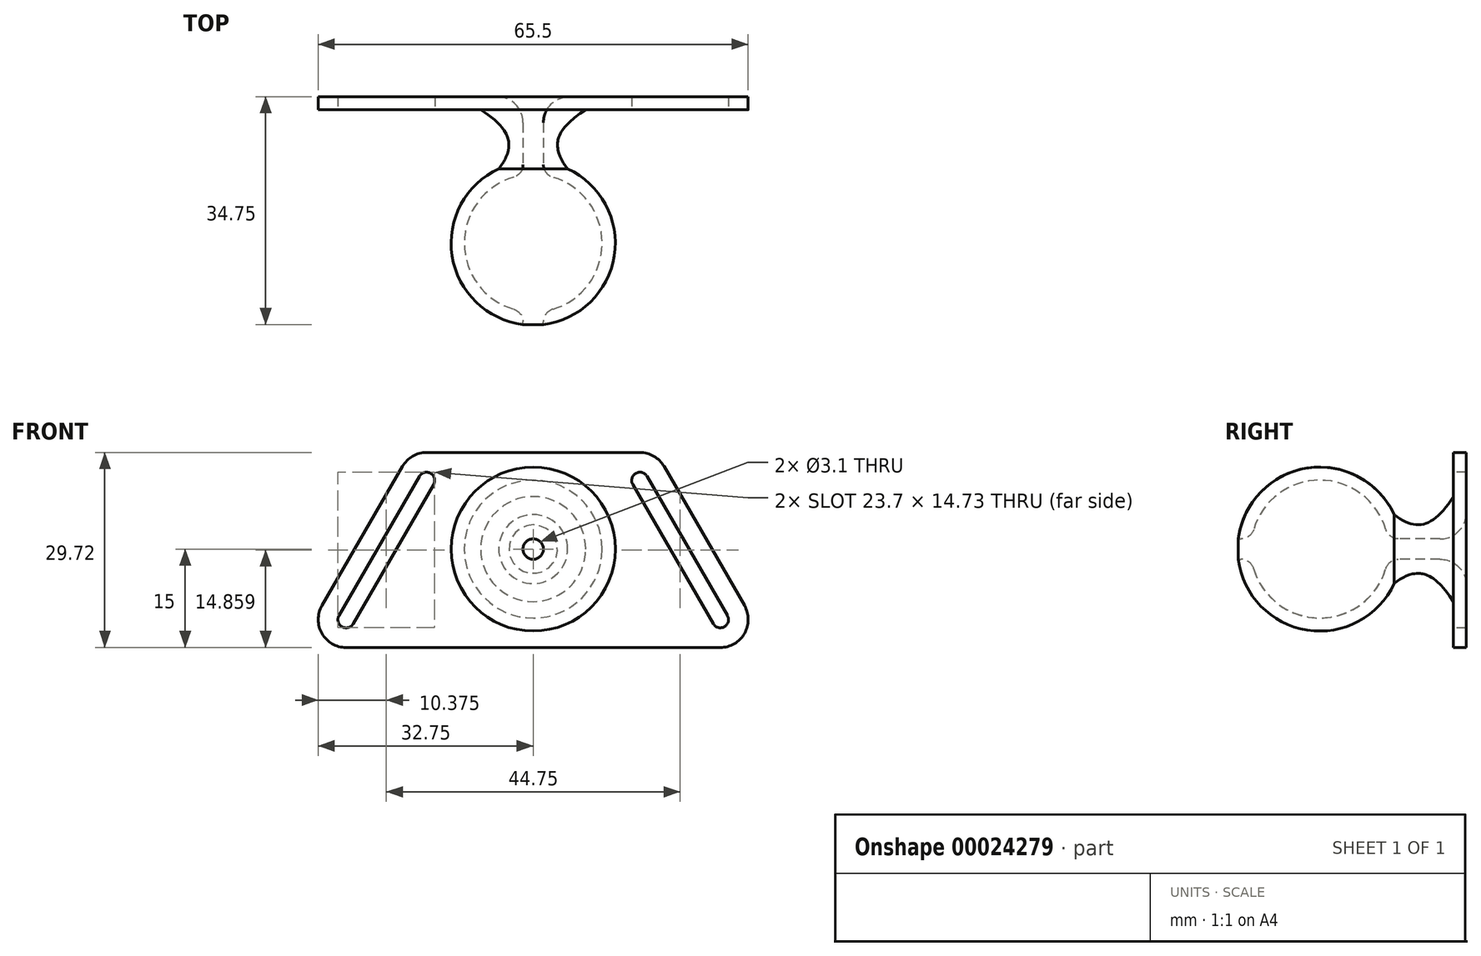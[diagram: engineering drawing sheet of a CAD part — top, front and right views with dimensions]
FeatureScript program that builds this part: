
annotation { "Feature Type Name" : "Feature", "Feature Type Description" : "" }
export const myFeature = defineFeature(function(context is Context, id is Id, definition is map)
    precondition{}
    {
        {
            var Q0;
            Q0=qCreatedBy(makeId("Front.planeOp"),FACE);
            var sketch = newSketch(context, id + "F0", { "sketchPlane" : qUnion([Q0])});
            skLineSegment(sketch, "E0", {"start": v(0, 0) * mm, "end": v(-28.5, 0) * mm});
            skLineSegment(sketch, "E1", {"start": v(0, 0) * mm, "end": v(0, 29.72) * mm});
            skLineSegment(sketch, "E2", {"start": v(-16.25, 25.47) * mm, "end": v(-28.5, 4.25) * mm, "construction": true});
            skCircle(sketch, "E3", {"center": v(-28.5, 4.25) * mm, "radius": 1.25 * mm});
            skCircle(sketch, "E4", {"center": v(-16.25, 25.47) * mm, "radius": 1.25 * mm});
            skLineSegment(sketch, "E5", {"start": v(-29.58, 4.87) * mm, "end": v(-17.33, 26.1) * mm});
            skLineSegment(sketch, "E6", {"start": v(-15.17, 24.84) * mm, "end": v(-27.42, 3.62) * mm});
            skCircle(sketch, "E7.0", {"center": v(-28.5, 4.25) * mm, "radius": 4.25 * mm});
            skCircle(sketch, "E8.0", {"center": v(-16.25, 25.47) * mm, "radius": 4.25 * mm});
            skLineSegment(sketch, "E9", {"start": v(-32.18, 6.37) * mm, "end": v(-19.93, 27.6) * mm});
            skLineSegment(sketch, "E10", {"start": v(-16.25, 29.72) * mm, "end": v(0, 29.72) * mm});
            skPoint(sketch, "E11", {"position": v(0, 15) * mm});
            skArc(sketch, "E12", {"start": v(0, 16.55) * mm, "mid": v(-1.55, 15) * mm, "end": v(0, 13.45) * mm});
            skSolve(sketch);
        }
        {
            var Q0;
            {var subQ3=sQuery(id+"F0.wireOp",EDGE,"E9");Q0=makeQuery(id+"F0.imprint","IMPRINT",FACE,{"disambiguationData":[TD([[makeQuery(id+"F0.imprint","IMPRINT",EDGE,{"derivedFrom":subQ3}),-1.0]])]});}
            var Q1;
            {var subQ5=sQuery(id+"F0.wireOp",EDGE,"E5");var subQ7=sQuery(id+"F0.wireOp",EDGE,"E3");var subQ9=makeQuery(id+"F0.imprint","INTERSECT",VERTEX,{"derivedFrom":[subQ7,subQ5]});Q1=makeQuery(id+"F0.imprint","IMPRINT",FACE,{"disambiguationData":[TD([[makeQuery(id+"F0.imprint","IMPRINT",EDGE,{"disambiguationData":[TD([[subQ9,-1.0]])],"derivedFrom":subQ7}),-1.0]])]});}
            var Q2;
            {var subQ4=sQuery(id+"F0.wireOp",EDGE,"E5");var subQ7=sQuery(id+"F0.wireOp",EDGE,"E4");var subQ9=makeQuery(id+"F0.imprint","INTERSECT",VERTEX,{"derivedFrom":[subQ7,subQ4]});Q2=makeQuery(id+"F0.imprint","IMPRINT",FACE,{"disambiguationData":[TD([[makeQuery(id+"F0.imprint","IMPRINT",EDGE,{"disambiguationData":[TD([[subQ9,1.0]])],"derivedFrom":subQ7}),-1.0]])]});}
            var Q3;
            {var subQ6=sQuery(id+"F0.wireOp",EDGE,"E0");Q3=makeQuery(id+"F0.imprint","IMPRINT",FACE,{"disambiguationData":[TD([[makeQuery(id+"F0.imprint","IMPRINT",EDGE,{"derivedFrom":subQ6}),-1.0]])]});}
            extrude(context, id + "F1", {"entities" : qUnion([Q0, Q1, Q2, Q3]), "oppositeDirection" : true, "depth" : 2 * mm});
        }
        {
            var Q0;
            Q0=makeQuery(id+"F1.opExtrude","SWEPT_BODY",BODY,{"disambiguationData":[OSD([sQuery(id+"F0.wireOp",EDGE,"E0"),sQuery(id+"F0.wireOp",EDGE,"E1"),sQuery(id+"F0.wireOp",EDGE,"E3"),sQuery(id+"F0.wireOp",EDGE,"E4"),sQuery(id+"F0.wireOp",EDGE,"E5"),sQuery(id+"F0.wireOp",EDGE,"E6"),sQuery(id+"F0.wireOp",EDGE,"E7.0"),sQuery(id+"F0.wireOp",EDGE,"E8.0"),sQuery(id+"F0.wireOp",EDGE,"E9"),sQuery(id+"F0.wireOp",EDGE,"E10")])]});
            var Q1;
            Q1=makeQuery(id+"F1.opExtrude","SWEPT_FACE",FACE,{"disambiguationData":[OSD([sQuery(id+"F0.wireOp",EDGE,"E1")])]});
            mirror(context, id + "F2", {"operationType" : NewBodyOperationType.ADD, "entities" : qUnion([Q0]), "mirrorPlane" : qUnion([Q1])});
        }
        {
            var Q0;
            Q0=qCreatedBy(makeId("Right.planeOp"),FACE);
            var sketch = newSketch(context, id + "F3", { "sketchPlane" : qUnion([Q0])});
            skLineSegment(sketch, "E13", {"start": v(0, 15) * mm, "end": v(-32.84, 15) * mm});
            skArc(sketch, "E14", {"start": v(-32.84, 15) * mm, "mid": v(-20.34, 2.5) * mm, "end": v(-7.84, 15) * mm});
            skLineSegment(sketch, "E15", {"start": v(-9, 15) * mm, "end": v(-9, 9.75) * mm});
            skFitSpline(sketch, "E16", {"points": [v(-9, 9.75) * mm, v(0, 7) * mm], "startDerivative": vector(10.27, 8.04) * mm, "endDerivative": vector(9.03, -14.12) * mm});
            skLineSegment(sketch, "E17", {"start": v(-32.75, 13.45) * mm, "end": v(0, 13.45) * mm});
            skPoint(sketch, "E18.0", {"position": v(0, 15) * mm});
            skLineSegment(sketch, "E19", {"start": v(0, 15) * mm, "end": v(0, 7) * mm});
            skLineSegment(sketch, "E20.0", {"start": v(0, 13.45) * mm, "end": v(0, 16.55) * mm});
            skCircle(sketch, "E21", {"center": v(-20.34, 15) * mm, "radius": 10.5 * mm});
            skSolve(sketch);
        }
        {
            var Q0;
            {var subQ4=sQuery(id+"F3.wireOp",EDGE,"E16");Q0=makeQuery(id+"F3.imprint","IMPRINT",FACE,{"disambiguationData":[TD([[makeQuery(id+"F3.imprint","IMPRINT",EDGE,{"derivedFrom":subQ4}),1.0]])]});}
            var Q1;
            {var subQ0=sQuery(id+"F3.wireOp",EDGE,"E17");var subQ3=sQuery(id+"F3.wireOp",EDGE,"E14");var subQ4=makeQuery(id+"F3.imprint","INTERSECT",VERTEX,{"derivedFrom":[subQ3,subQ0]});Q1=makeQuery(id+"F3.imprint","IMPRINT",FACE,{"disambiguationData":[TD([[makeQuery(id+"F3.imprint","IMPRINT",EDGE,{"disambiguationData":[TD([[subQ4,1.0]])],"derivedFrom":subQ0}),-1.0]])]});}
            var Q2;
            {var subQ3=sQuery(id+"F3.wireOp",EDGE,"bf7e747b-2e18-4020-b302-44ba4e78f57e");var subQ5=sQuery(id+"F3.wireOp",EDGE,"E14");var subQ6=makeQuery(id+"F3.imprint","INTERSECT",VERTEX,{"derivedFrom":[subQ5,subQ3]});Q2=makeQuery(id+"F3.imprint","IMPRINT",FACE,{"disambiguationData":[TD([[makeQuery(id+"F3.imprint","IMPRINT",EDGE,{"disambiguationData":[TD([[subQ6,1.0]])],"derivedFrom":subQ3}),1.0]])]});}
            var Q3;
            {var subQ1=sQuery(id+"F3.wireOp",EDGE,"E17");var subQ6=sQuery(id+"F3.wireOp",EDGE,"E14");var subQ7=makeQuery(id+"F3.imprint","INTERSECT",VERTEX,{"disambiguationData":[OD(0.0)],"derivedFrom":[subQ6,subQ1]});Q3=makeQuery(id+"F3.imprint","IMPRINT",FACE,{"disambiguationData":[TD([[makeQuery(id+"F3.imprint","IMPRINT",EDGE,{"disambiguationData":[TD([[subQ7,-1.0]])],"derivedFrom":subQ1}),-1.0]])]});}
            var Q4;
            Q4=sQuery(id+"F3.wireOp",EDGE,"E13");
            revolve(context, id + "F4", {"operationType" : NewBodyOperationType.ADD, "entities" : qUnion([Q0, Q1, Q2, Q3]), "axis" : qUnion([Q4]), "revolveType" : RevolveType.FULL});
        }
        {
            var Q0;
            {var subQ0=makeQuery(id+"F1.opExtrude","CAP_EDGE",EDGE,{"disambiguationData":[OSD([sQuery(id+"F0.wireOp",EDGE,"E12")])],"isStart":false});Q0=makeQuery(id+"F2.boolean.opBoolean","MERGE",EDGE,{"derivedFrom":[subQ0,makeQuery(id+"F2.opPattern","COPY",EDGE,{"derivedFrom":subQ0,"instanceName":"1"})]});}
            var Q1;
            Q1=makeQuery(id+"F4.opRevolve","SWEPT_EDGE",EDGE,{"disambiguationData":[OSD([sQuery(id+"F3.wireOp",EDGE,"E16"),sQuery(id+"F3.wireOp",EDGE,"E19")])]});
            fillet(context, id + "F5", {"entities" : qUnion([Q0, Q1]), "radius" : 4 * mm, "tangentPropagation" : true, "allowEdgeOverflow" : false});
        }
        {
            var Q0;
            {var subQ0=sQuery(id+"F3.wireOp",EDGE,"E17");var subQ1=sQuery(id+"F3.wireOp",EDGE,"E21");Q0=makeQuery(id+"F4.opRevolve","SWEPT_EDGE",EDGE,{"disambiguationData":[OSD([subQ0,subQ1]),TDD([makeQuery(id+"F3.imprint","INTERSECT",VERTEX,{"disambiguationData":[OD(1.0)],"derivedFrom":[subQ0,subQ1]})])]});}
            var Q1;
            {var subQ0=sQuery(id+"F3.wireOp",EDGE,"E17");var subQ1=sQuery(id+"F3.wireOp",EDGE,"E21");Q1=makeQuery(id+"F4.opRevolve","SWEPT_EDGE",EDGE,{"disambiguationData":[OSD([subQ0,subQ1]),TDD([makeQuery(id+"F3.imprint","INTERSECT",VERTEX,{"disambiguationData":[OD(0.0)],"derivedFrom":[subQ0,subQ1]})])]});}
            fillet(context, id + "F6", {"entities" : qUnion([Q0, Q1]), "radius" : 2 * mm, "tangentPropagation" : true, "allowEdgeOverflow" : false});
        }
    });
